# Revit family: BE_84769_de_DE
name_source: partatom
category: Leuchten
units: mm (PartAtom-declared; Revit-internal decimal feet)

## family parameters
Basisbauteil = Fläche
Beim Laden mit Abzugskörper schneiden = Ja
Bemaßung runder Anschluss = Durchmesser verwenden
Gemeinsam genutzt = Nein
Lichtquelle = Nein
Raumberechnungspunkt = Ja
Teiletyp = Normal

## types (1)
- BEGA_84769_Grafit_K3
    AC/DC = AC
    Aktualisierung = 2022-05-19T04:00:07
    Anschlussleitung = 5.0 m X05RN-F FEP 2 × 1² + 1G2,5²
    BEGA_Dummy = Nein
    BEGA_IES1 = Ja
    BEGA_IES2 = Ja
    BEGA_IES3 = Ja
    BEGA_Intern = Ja
    BEGA_Intern_Konstruktion = Ja
    BEGA_Intern_an = Ja
    BEGA_Intern_aus = Ja
    Befestigungsabstand = 67 mm
    Befestigungsbohrung = Ø 4,8 mm
    Beschreibung = Scheinwerfer BEGA UniLink
    Beschreibung_Sonderanfertigung = Hier können Sie Informationen zur Sonderanfertigung eintragen.
    Bestellnummer = 84769K3
    CE_Konformität = ja
    Energieeffizienzklasse = LED A++ - A
    Farbtemperatur = 3000 K
    Farbwiedergabeindex = CRI > 90
    Frequenz = 50-60 Hz
    Gewicht = 1.9 kg
    Hersteller = BEGA
    LED_Modulbezeichnung = LED-1157/930
    Lampe = LED 8.2 W
    Lampenlichtstrom = 970 lm
    Lastklassifizierung = Beleuchtung
    Lebensdauerkriterien = L70B50 @ 25 °C = 200000 h
    Leuchtenlichtstrom = 773 lm
    Logo = BEGA_Logo.png
    M_A = Nein
    M_G = Ja
    M_W = Nein
    Material_06 = BEGA_Oberfläche_Edelstahl_gebürstet
    Material_09 = BEGA_Glas_klar
    Material_11 = BEGA_Glas_opal
    Material_13 = BEGA_Kunststoff_matt
    Material_15 = BEGA_Leuchtmedium_matt
    Material_17 = BEGA_Reflektor
    Material_18 = BEGA_Gummi_schwarz
    Modell = 84769K3
    Produktdatenblatt = https://cdn.bega.com
    Scheinlast = 0 VA
    Schutzart = IP 65
    Schutzklasse = I
    Sonderanfertigung = Nein
    Spannung = 240 V
    Strom = 0,05 A
    URL = https://www.bega.com
    Umgebungstemperatur = 25 °C
    Vorgabe-Ansicht = 0 mm  [stored 0 ft]

note: [stored X ft] marks values corroborated as IEEE doubles in the binary element streams (Revit-internal decimal feet)

## geometry (parser evidence)
native form markers: Blend x9, Sweep x9
no freeform markers — native parametric forms only
